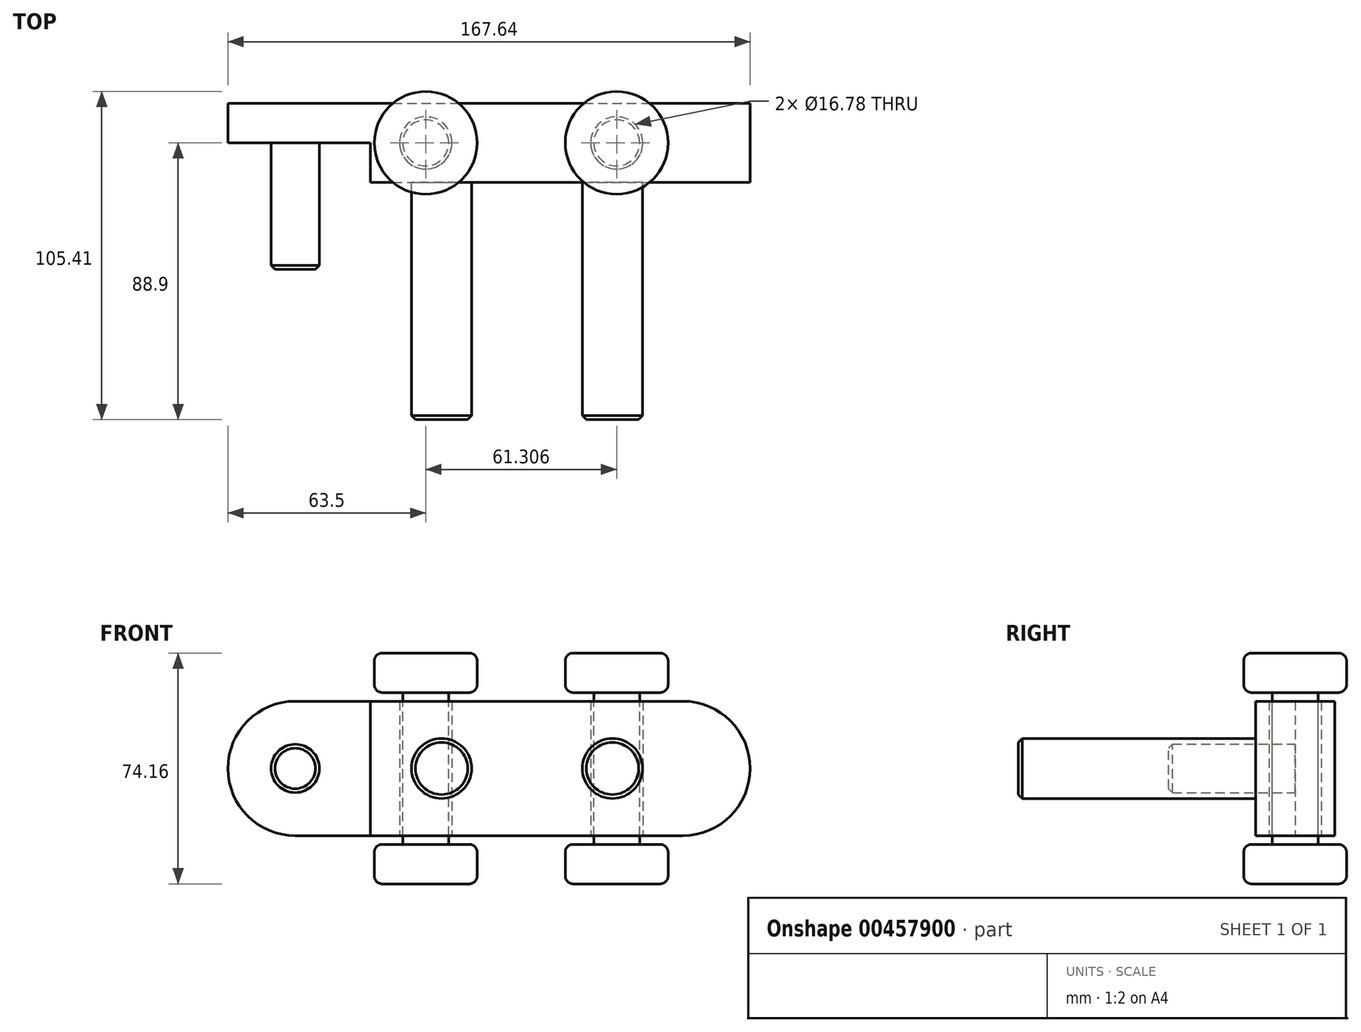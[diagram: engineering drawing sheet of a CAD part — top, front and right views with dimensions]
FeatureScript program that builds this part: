
annotation { "Feature Type Name" : "Feature", "Feature Type Description" : "" }
export const myFeature = defineFeature(function(context is Context, id is Id, definition is map)
    precondition{}
    {
        {
            var Q0;
            Q0=qCreatedBy(makeId("Front.planeOp"),FACE);
            var sketch = newSketch(context, id + "F0", { "sketchPlane" : qUnion([Q0])});
            skLineSegment(sketch, "E0", {"start": v(0, 21.6) * mm, "end": v(124.46, 21.6) * mm});
            skArc(sketch, "E1", {"start": v(124.46, -21.59) * mm, "mid": v(146.05, 0) * mm, "end": v(124.46, 21.59) * mm});
            skLineSegment(sketch, "E2", {"start": v(124.46, -21.59) * mm, "end": v(0, -21.6) * mm});
            skArc(sketch, "E3", {"start": v(0, 21.6) * mm, "mid": v(-21.6, 0) * mm, "end": v(0, -21.6) * mm});
            skCircle(sketch, "E4", {"center": v(101.85, 0) * mm, "radius": 9.65 * mm});
            skCircle(sketch, "E5", {"center": v(46.99, 0) * mm, "radius": 9.65 * mm});
            skLineSegment(sketch, "E6", {"start": v(24.13, 21.6) * mm, "end": v(24.13, -21.6) * mm});
            skSolve(sketch);
        }
        {
            var Q0;
            {var subQ1=sQuery(id+"F0.wireOp",EDGE,"BVxJP915-IevX-kX70-ISTD-4brrsj3BFpD8");Q0=makeQuery(id+"F0.imprint","IMPRINT",FACE,{"disambiguationData":[TD([[makeQuery(id+"F0.imprint","IMPRINT",EDGE,{"derivedFrom":subQ1}),1.0]])]});}
            var Q1;
            {var subQ0=sQuery(id+"F0.wireOp",EDGE,"E1");Q1=makeQuery(id+"F0.imprint","IMPRINT",FACE,{"disambiguationData":[TD([[makeQuery(id+"F0.imprint","IMPRINT",EDGE,{"derivedFrom":subQ0}),1.0]])]});}
            extrude(context, id + "F1", {"entities" : qUnion([Q0, Q1]), "depth" : 25.4 * mm, "offsetDistance" : 25.4 * mm});
        }
        {
            var Q0;
            Q0=makeQuery(id+"F0.imprint","IMPRINT",FACE,{"disambiguationData":[TD([[makeQuery(id+"F0.imprint","IMPRINT",EDGE,{"derivedFrom":sQuery(id+"F0.wireOp",EDGE,"E3")}),1.0]])]});
            extrude(context, id + "F2", {"entities" : qUnion([Q0]), "operationType" : NewBodyOperationType.ADD, "depth" : 12.7 * mm, "offsetDistance" : 25.4 * mm});
        }
        {
            var Q0;
            Q0=makeQuery(id+"F0.imprint","IMPRINT",FACE,{"disambiguationData":[TD([[makeQuery(id+"F0.imprint","IMPRINT",EDGE,{"derivedFrom":sQuery(id+"F0.wireOp",EDGE,"E5")}),1.0]])]});
            var Q1;
            Q1=makeQuery(id+"F0.imprint","IMPRINT",FACE,{"disambiguationData":[TD([[makeQuery(id+"F0.imprint","IMPRINT",EDGE,{"derivedFrom":sQuery(id+"F0.wireOp",EDGE,"E4")}),1.0]])]});
            extrude(context, id + "F3", {"entities" : qUnion([Q0, Q1]), "operationType" : NewBodyOperationType.ADD, "depth" : 101.6 * mm, "offsetDistance" : 25.4 * mm});
        }
        {
            var Q0;
            {var subQ0=sQuery(id+"F0.wireOp",EDGE,"E2");Q0=makeQuery(id+"FQ4Pn4z8IeTTJgR_0.boolean.opBoolean","MERGE",FACE,{"derivedFrom":[makeQuery(id+"F1.opExtrude","SWEPT_FACE",FACE,{"disambiguationData":[OSD([subQ0])]}),makeQuery(id+"FQ4Pn4z8IeTTJgR_0.opExtrude","SWEPT_FACE",FACE,{"disambiguationData":[OSD([subQ0])]})]});}
            var sketch = newSketch(context, id + "F4", { "sketchPlane" : qUnion([Q0])});
            skLineSegment(sketch, "E7.0", {"start": v(37.34, 101.6) * mm, "end": v(56.64, 101.6) * mm});
            skLineSegment(sketch, "E8.0", {"start": v(124.46, 25.4) * mm, "end": v(24.13, 25.4) * mm});
            skLineSegment(sketch, "E9.0", {"start": v(92.2, 101.6) * mm, "end": v(111.5, 101.6) * mm});
            skCircle(sketch, "E10", {"center": v(41.9, 12.7) * mm, "radius": 8.4 * mm});
            skCircle(sketch, "E11", {"center": v(103.22, 12.7) * mm, "radius": 8.4 * mm});
            skSolve(sketch);
        }
        {
            var Q0;
            Q0=makeQuery(id+"F2.opExtrude","CAP_FACE",FACE,{"disambiguationData":[OSD([sQuery(id+"F0.wireOp",EDGE,"E3"),sQuery(id+"F0.wireOp",EDGE,"BVxJP915-IevX-kX70-ISTD-4brrsj3BFpD8")])],"isStart":false});
            var sketch = newSketch(context, id + "F5", { "sketchPlane" : qUnion([Q0])});
            skPoint(sketch, "E12.centerSnap0", {"position": v(24.13, 0) * mm});
            skCircle(sketch, "E13", {"center": v(0, 0) * mm, "radius": 7.77 * mm});
            skSolve(sketch);
        }
        {
            var Q0;
            Q0 = qSketchRegion(id + "F5", true);
            extrude(context, id + "F6", {"entities" : qUnion([Q0]), "operationType" : NewBodyOperationType.ADD, "depth" : 40.64 * mm, "offsetDistance" : 25.4 * mm});
        }
        {
            var Q0;
            Q0=makeQuery(id+"F4.imprint","IMPRINT",FACE,{"disambiguationData":[TD([[makeQuery(id+"F4.imprint","IMPRINT",EDGE,{"derivedFrom":sQuery(id+"F4.wireOp",EDGE,"E11")}),1.0]])]});
            var Q1;
            Q1=makeQuery(id+"F4.imprint","IMPRINT",FACE,{"disambiguationData":[TD([[makeQuery(id+"F4.imprint","IMPRINT",EDGE,{"derivedFrom":sQuery(id+"F4.wireOp",EDGE,"E10")}),1.0]])]});
            extrude(context, id + "F7", {"entities" : qUnion([Q0, Q1]), "operationType" : NewBodyOperationType.REMOVE, "endBound" : BoundingType.THROUGH_ALL, "oppositeDirection" : true, "depth" : 5.08 * mm, "offsetDistance" : 25.4 * mm});
        }
        {
            var Q0;
            Q0=qCreatedBy(makeId("Top.planeOp"),FACE);
            var sketch = newSketch(context, id + "F8", { "sketchPlane" : qUnion([Q0])});
            skCircle(sketch, "E14.0", {"center": v(41.9, -12.7) * mm, "radius": 8.4 * mm});
            skCircle(sketch, "E15.0", {"center": v(103.22, -12.7) * mm, "radius": 8.4 * mm});
            skCircle(sketch, "E16", {"center": v(103.22, -12.7) * mm, "radius": 7.37 * mm});
            skCircle(sketch, "E17", {"center": v(41.9, -12.7) * mm, "radius": 7.37 * mm});
            skSolve(sketch);
        }
        {
            var Q0;
            Q0=makeQuery(id+"F8.imprint","IMPRINT",FACE,{"disambiguationData":[TD([[makeQuery(id+"F8.imprint","IMPRINT",EDGE,{"derivedFrom":sQuery(id+"F8.wireOp",EDGE,"E17")}),1.0]])]});
            var Q1;
            Q1=makeQuery(id+"F8.imprint","IMPRINT",FACE,{"disambiguationData":[TD([[makeQuery(id+"F8.imprint","IMPRINT",EDGE,{"derivedFrom":sQuery(id+"F8.wireOp",EDGE,"E16")}),1.0]])]});
            extrude(context, id + "F9", {"entities" : qUnion([Q0, Q1]), "operationType" : NewBodyOperationType.ADD, "endBound" : BoundingType.SYMMETRIC, "oppositeDirection" : true, "depth" : 48.77 * mm, "offsetDistance" : 25.4 * mm});
        }
        {
            var Q0;
            Q0=makeQuery(id+"F9.opExtrude","CAP_FACE",FACE,{"disambiguationData":[OSD([sQuery(id+"F8.wireOp",EDGE,"E17")])],"isStart":false});
            var sketch = newSketch(context, id + "F10", { "sketchPlane" : qUnion([Q0])});
            skCircle(sketch, "E18", {"center": v(41.9, 12.7) * mm, "radius": 16.51 * mm});
            skCircle(sketch, "E19", {"center": v(103.22, 12.7) * mm, "radius": 16.51 * mm});
            skSolve(sketch);
        }
        {
            var Q0;
            Q0=makeQuery(id+"F10.imprint","IMPRINT",FACE,{"disambiguationData":[TD([[makeQuery(id+"F10.imprint","IMPRINT",EDGE,{"derivedFrom":sQuery(id+"F10.wireOp",EDGE,"E18")}),1.0]])]});
            var Q1;
            Q1=makeQuery(id+"F10.imprint","IMPRINT",FACE,{"disambiguationData":[TD([[makeQuery(id+"F10.imprint","IMPRINT",EDGE,{"derivedFrom":makeQuery(id+"F9.opExtrude","CAP_EDGE",EDGE,{"disambiguationData":[OSD([sQuery(id+"F8.wireOp",EDGE,"E17")])],"isStart":false})}),-1.0]])]});
            var Q2;
            Q2=makeQuery(id+"F10.imprint","IMPRINT",FACE,{"disambiguationData":[TD([[makeQuery(id+"F10.imprint","IMPRINT",EDGE,{"derivedFrom":sQuery(id+"F10.wireOp",EDGE,"E19")}),1.0]])]});
            extrude(context, id + "F11", {"entities" : qUnion([Q0, Q1, Q2]), "depth" : 12.7 * mm, "offsetDistance" : 25.4 * mm});
        }
        {
            var Q0;
            Q0=makeQuery(id+"F11.opExtrude","CAP_EDGE",EDGE,{"disambiguationData":[OSD([sQuery(id+"F10.wireOp",EDGE,"E18")])],"isStart":false});
            var Q1;
            Q1=makeQuery(id+"F11.opExtrude","CAP_EDGE",EDGE,{"disambiguationData":[OSD([sQuery(id+"F10.wireOp",EDGE,"E18")])],"isStart":true});
            var Q2;
            Q2=makeQuery(id+"F11.opExtrude","CAP_EDGE",EDGE,{"disambiguationData":[OSD([sQuery(id+"F10.wireOp",EDGE,"E19")])],"isStart":false});
            var Q3;
            Q3=makeQuery(id+"F11.opExtrude","CAP_EDGE",EDGE,{"disambiguationData":[OSD([sQuery(id+"F10.wireOp",EDGE,"E19")])],"isStart":true});
            fillet(context, id + "F12", {"entities" : qUnion([Q0, Q1, Q2, Q3]), "radius" : 2.54 * mm, "tangentPropagation" : true, "allowEdgeOverflow" : false});
        }
        {
            var Q0;
            Q0=makeQuery(id+"F9.opExtrude","SWEPT_BODY",BODY,{"disambiguationData":[OSD([sQuery(id+"F8.wireOp",EDGE,"E17")])]});
            var Q1;
            Q1=makeQuery(id+"F11.opExtrude","SWEPT_BODY",BODY,{"disambiguationData":[OSD([sQuery(id+"F10.wireOp",EDGE,"E18")])]});
            var Q2;
            Q2=makeQuery(id+"F11.opExtrude","SWEPT_BODY",BODY,{"disambiguationData":[OSD([sQuery(id+"F10.wireOp",EDGE,"E19")])]});
            var Q3;
            Q3=makeQuery(id+"F9.opExtrude","SWEPT_BODY",BODY,{"disambiguationData":[OSD([sQuery(id+"F8.wireOp",EDGE,"E16")])]});
            var Q4;
            Q4=qCreatedBy(makeId("Top.planeOp"),FACE);
            mirror(context, id + "F13", {"operationType" : NewBodyOperationType.ADD, "entities" : qUnion([Q0, Q1, Q2, Q3]), "mirrorPlane" : qUnion([Q4])});
        }
        {
            var Q0;
            Q0=makeQuery(id+"F3.opExtrude","CAP_EDGE",EDGE,{"disambiguationData":[OSD([sQuery(id+"F0.wireOp",EDGE,"E4")])],"isStart":false});
            var Q1;
            Q1=makeQuery(id+"F3.opExtrude","CAP_EDGE",EDGE,{"disambiguationData":[OSD([sQuery(id+"F0.wireOp",EDGE,"E5")])],"isStart":false});
            var Q2;
            Q2=makeQuery(id+"F6.opExtrude","CAP_EDGE",EDGE,{"disambiguationData":[OSD([sQuery(id+"F5.wireOp",EDGE,"E13")])],"isStart":false});
            chamfer(context, id + "F14", {"entities" : qUnion([Q0, Q1, Q2]), "width" : 1.27 * mm, "tangentPropagation" : true});
        }
    });
